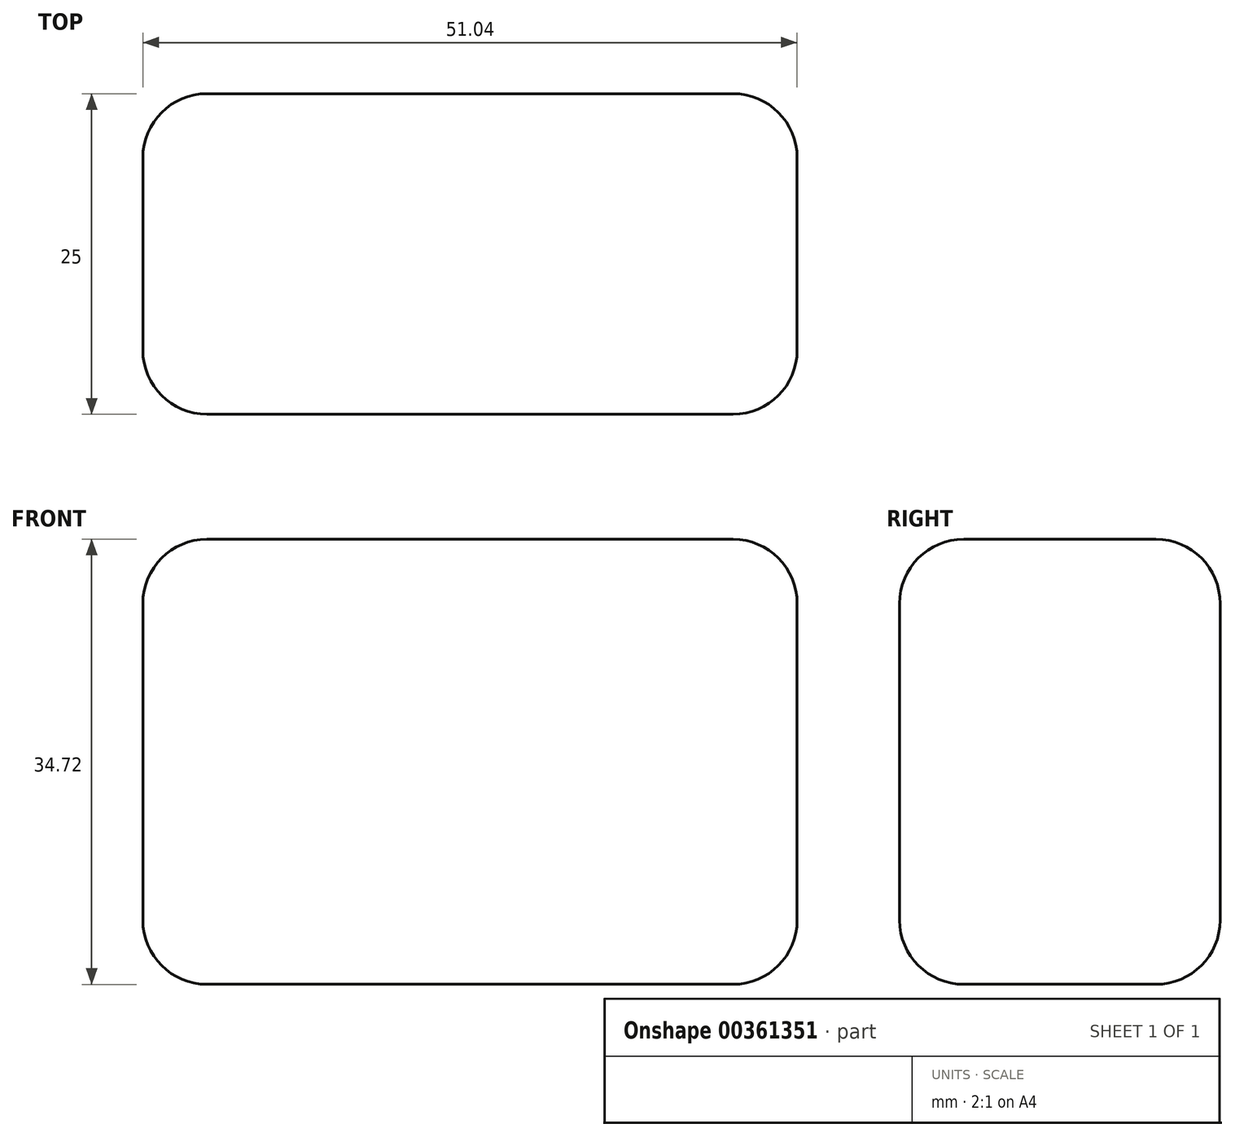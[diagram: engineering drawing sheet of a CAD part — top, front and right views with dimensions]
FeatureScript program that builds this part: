
annotation { "Feature Type Name" : "Feature", "Feature Type Description" : "" }
export const myFeature = defineFeature(function(context is Context, id is Id, definition is map)
    precondition{}
    {
        {
            var Q0;
            Q0=qCreatedBy(makeId("Front.planeOp"),FACE);
            var sketch = newSketch(context, id + "F0", { "sketchPlane" : qUnion([Q0])});
            skLineSegment(sketch, "E0.bottom", {"start": v(-25.52, 17.36) * mm, "end": v(25.52, 17.36) * mm});
            skLineSegment(sketch, "E0.top", {"start": v(-25.52, -17.36) * mm, "end": v(25.52, -17.36) * mm});
            skLineSegment(sketch, "E0.left", {"start": v(-25.52, 17.36) * mm, "end": v(-25.52, -17.36) * mm});
            skLineSegment(sketch, "E0.right", {"start": v(25.52, 17.36) * mm, "end": v(25.52, -17.36) * mm});
            skPoint(sketch, "E0.middle", {"position": v(0, 0) * mm});
            skSolve(sketch);
        }
        {
            var Q0;
            Q0 = qSketchRegion(id + "F0", true);
            extrude(context, id + "F1", {"entities" : qUnion([Q0]), "depth" : 25 * mm, "hasDraft" : true, "draftAngle" : 0 * degree});
        }
        {
            var Q0;
            Q0=makeQuery(id+"F1.opExtrude","CAP_EDGE",EDGE,{"disambiguationData":[OSD([sQuery(id+"F0.wireOp",EDGE,"E0.bottom")])],"isStart":false});
            var Q1;
            Q1=makeQuery(id+"F1.opExtrude","CAP_EDGE",EDGE,{"disambiguationData":[OSD([sQuery(id+"F0.wireOp",EDGE,"E0.bottom")])],"isStart":true});
            var Q2;
            Q2=makeQuery(id+"F1.opExtrude","SWEPT_EDGE",EDGE,{"disambiguationData":[OSD([sQuery(id+"F0.wireOp",EDGE,"E0.bottom"),sQuery(id+"F0.wireOp",EDGE,"E0.left")])]});
            var Q3;
            Q3=makeQuery(id+"F1.opExtrude","SWEPT_EDGE",EDGE,{"disambiguationData":[OSD([sQuery(id+"F0.wireOp",EDGE,"E0.bottom"),sQuery(id+"F0.wireOp",EDGE,"E0.right")])]});
            fillet(context, id + "F2", {"entities" : qUnion([Q0, Q1, Q2, Q3]), "radius" : 5 * mm, "tangentPropagation" : true, "allowEdgeOverflow" : false});
        }
        {
            var Q0;
            Q0=makeQuery(id+"F1.opExtrude","SWEPT_EDGE",EDGE,{"disambiguationData":[OSD([sQuery(id+"F0.wireOp",EDGE,"E0.top"),sQuery(id+"F0.wireOp",EDGE,"E0.left")])]});
            var Q1;
            {var subQ0=sQuery(id+"F0.wireOp",EDGE,"E0.bottom");Q1=makeQuery(id+"F2.opFillet","BLEND_EDGE",EDGE,{"blendedFrom":[makeQuery(id+"F1.opExtrude","CAP_EDGE",EDGE,{"disambiguationData":[OSD([subQ0])],"isStart":true}),makeQuery(id+"F1.opExtrude","CAP_FACE",FACE,{"disambiguationData":[OSD([subQ0,sQuery(id+"F0.wireOp",EDGE,"E0.top"),sQuery(id+"F0.wireOp",EDGE,"E0.left"),sQuery(id+"F0.wireOp",EDGE,"E0.right")])],"isStart":true})],"blendedInto":[makeQuery(id+"F1.opExtrude","CAP_FACE",FACE,{"disambiguationData":[OSD([subQ0,sQuery(id+"F0.wireOp",EDGE,"E0.top"),sQuery(id+"F0.wireOp",EDGE,"E0.left"),sQuery(id+"F0.wireOp",EDGE,"E0.right")])],"isStart":true})]});}
            var Q2;
            Q2=makeQuery(id+"F1.opExtrude","SWEPT_EDGE",EDGE,{"disambiguationData":[OSD([sQuery(id+"F0.wireOp",EDGE,"E0.top"),sQuery(id+"F0.wireOp",EDGE,"E0.right")])]});
            var Q3;
            Q3=makeQuery(id+"F1.opExtrude","CAP_EDGE",EDGE,{"disambiguationData":[OSD([sQuery(id+"F0.wireOp",EDGE,"E0.top")])],"isStart":false});
            fillet(context, id + "F3", {"entities" : qUnion([Q0, Q1, Q2, Q3]), "radius" : 5 * mm, "tangentPropagation" : true, "allowEdgeOverflow" : false});
        }
        {
            var Q0;
            {var subQ0=sQuery(id+"F0.wireOp",EDGE,"E0.top");Q0=makeQuery(id+"F3.opFillet","BLEND_EDGE",EDGE,{"blendedFrom":[makeQuery(id+"F1.opExtrude","SWEPT_EDGE",EDGE,{"disambiguationData":[OSD([subQ0,sQuery(id+"F0.wireOp",EDGE,"E0.left")])]}),makeQuery(id+"F1.opExtrude","SWEPT_FACE",FACE,{"disambiguationData":[OSD([subQ0])]})],"blendedInto":[makeQuery(id+"F1.opExtrude","SWEPT_FACE",FACE,{"disambiguationData":[OSD([subQ0])]})]});}
            var Q1;
            {var subQ0=sQuery(id+"F0.wireOp",EDGE,"E0.top");Q1=makeQuery(id+"F3.opFillet","BLEND_EDGE",EDGE,{"blendedFrom":[makeQuery(id+"F1.opExtrude","SWEPT_EDGE",EDGE,{"disambiguationData":[OSD([subQ0,sQuery(id+"F0.wireOp",EDGE,"E0.right")])]}),makeQuery(id+"F1.opExtrude","SWEPT_FACE",FACE,{"disambiguationData":[OSD([subQ0])]})],"blendedInto":[makeQuery(id+"F1.opExtrude","SWEPT_FACE",FACE,{"disambiguationData":[OSD([subQ0])]})]});}
            var Q2;
            Q2=makeQuery(id+"F1.opExtrude","CAP_EDGE",EDGE,{"disambiguationData":[OSD([sQuery(id+"F0.wireOp",EDGE,"E0.top")])],"isStart":true});
            fillet(context, id + "F4", {"entities" : qUnion([Q0, Q1, Q2]), "radius" : 5 * mm, "tangentPropagation" : true, "allowEdgeOverflow" : false});
        }
        {
            var Q0;
            {var subQ0=sQuery(id+"F0.wireOp",EDGE,"E0.top");Q0=makeQuery(id+"F3.opFillet","BLEND_EDGE",EDGE,{"blendedFrom":[makeQuery(id+"F1.opExtrude","CAP_EDGE",EDGE,{"disambiguationData":[OSD([subQ0])],"isStart":false}),makeQuery(id+"F1.opExtrude","CAP_FACE",FACE,{"disambiguationData":[OSD([sQuery(id+"F0.wireOp",EDGE,"E0.bottom"),subQ0,sQuery(id+"F0.wireOp",EDGE,"E0.left"),sQuery(id+"F0.wireOp",EDGE,"E0.right")])],"isStart":false})],"blendedInto":[makeQuery(id+"F1.opExtrude","CAP_FACE",FACE,{"disambiguationData":[OSD([sQuery(id+"F0.wireOp",EDGE,"E0.bottom"),subQ0,sQuery(id+"F0.wireOp",EDGE,"E0.left"),sQuery(id+"F0.wireOp",EDGE,"E0.right")])],"isStart":false})]});}
            var Q1;
            {var subQ0=sQuery(id+"F0.wireOp",EDGE,"E0.bottom");Q1=makeQuery(id+"F2.opFillet","BLEND_EDGE",EDGE,{"blendedFrom":[makeQuery(id+"F1.opExtrude","CAP_EDGE",EDGE,{"disambiguationData":[OSD([subQ0])],"isStart":false}),makeQuery(id+"F1.opExtrude","CAP_FACE",FACE,{"disambiguationData":[OSD([subQ0,sQuery(id+"F0.wireOp",EDGE,"E0.top"),sQuery(id+"F0.wireOp",EDGE,"E0.left"),sQuery(id+"F0.wireOp",EDGE,"E0.right")])],"isStart":false})],"blendedInto":[makeQuery(id+"F1.opExtrude","CAP_FACE",FACE,{"disambiguationData":[OSD([subQ0,sQuery(id+"F0.wireOp",EDGE,"E0.top"),sQuery(id+"F0.wireOp",EDGE,"E0.left"),sQuery(id+"F0.wireOp",EDGE,"E0.right")])],"isStart":false})]});}
            var Q2;
            Q2=makeQuery(id+"F1.opExtrude","CAP_EDGE",EDGE,{"disambiguationData":[OSD([sQuery(id+"F0.wireOp",EDGE,"E0.right")])],"isStart":false});
            var Q3;
            Q3=makeQuery(id+"F1.opExtrude","CAP_EDGE",EDGE,{"disambiguationData":[OSD([sQuery(id+"F0.wireOp",EDGE,"E0.left")])],"isStart":false});
            fillet(context, id + "F5", {"entities" : qUnion([Q0, Q1, Q2, Q3]), "radius" : 5 * mm, "tangentPropagation" : true, "allowEdgeOverflow" : false});
        }
    });
